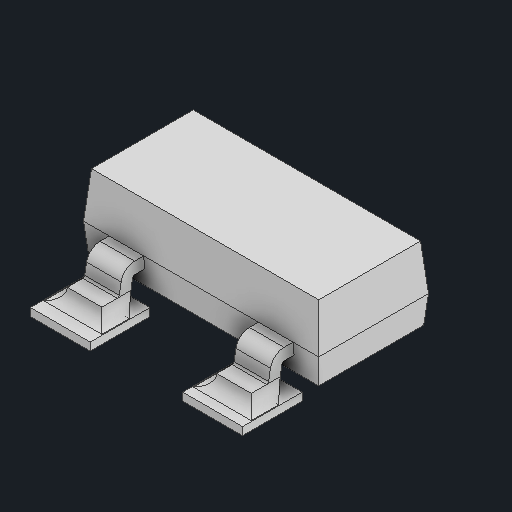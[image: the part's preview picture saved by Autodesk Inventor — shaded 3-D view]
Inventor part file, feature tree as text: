
AUTODESK INVENTOR PART (.ipt)
format: ipt  version: 2023 (Build 270158000, 158)  size: 146,944 bytes
history: native  units: in
note: dims shown in document units (in); Inventor stores cm internally (conversion verified against a paired STEP export)
features: fillet x1
ambient origin geometry x8: Origin, YZ Plane, XZ Plane, XY Plane, X Axis, Y Axis, Z Axis, Center Point
bodies: Solid1 (feature_tree)
feature tree (1):
  fillet  "Fillet1"  [1 undecoded]
note: 1 required parameter value undecoded (feature->parameter linkage not recoverable at this tier; creation-order binding heuristic only, values carry confidence <= 0.55)
